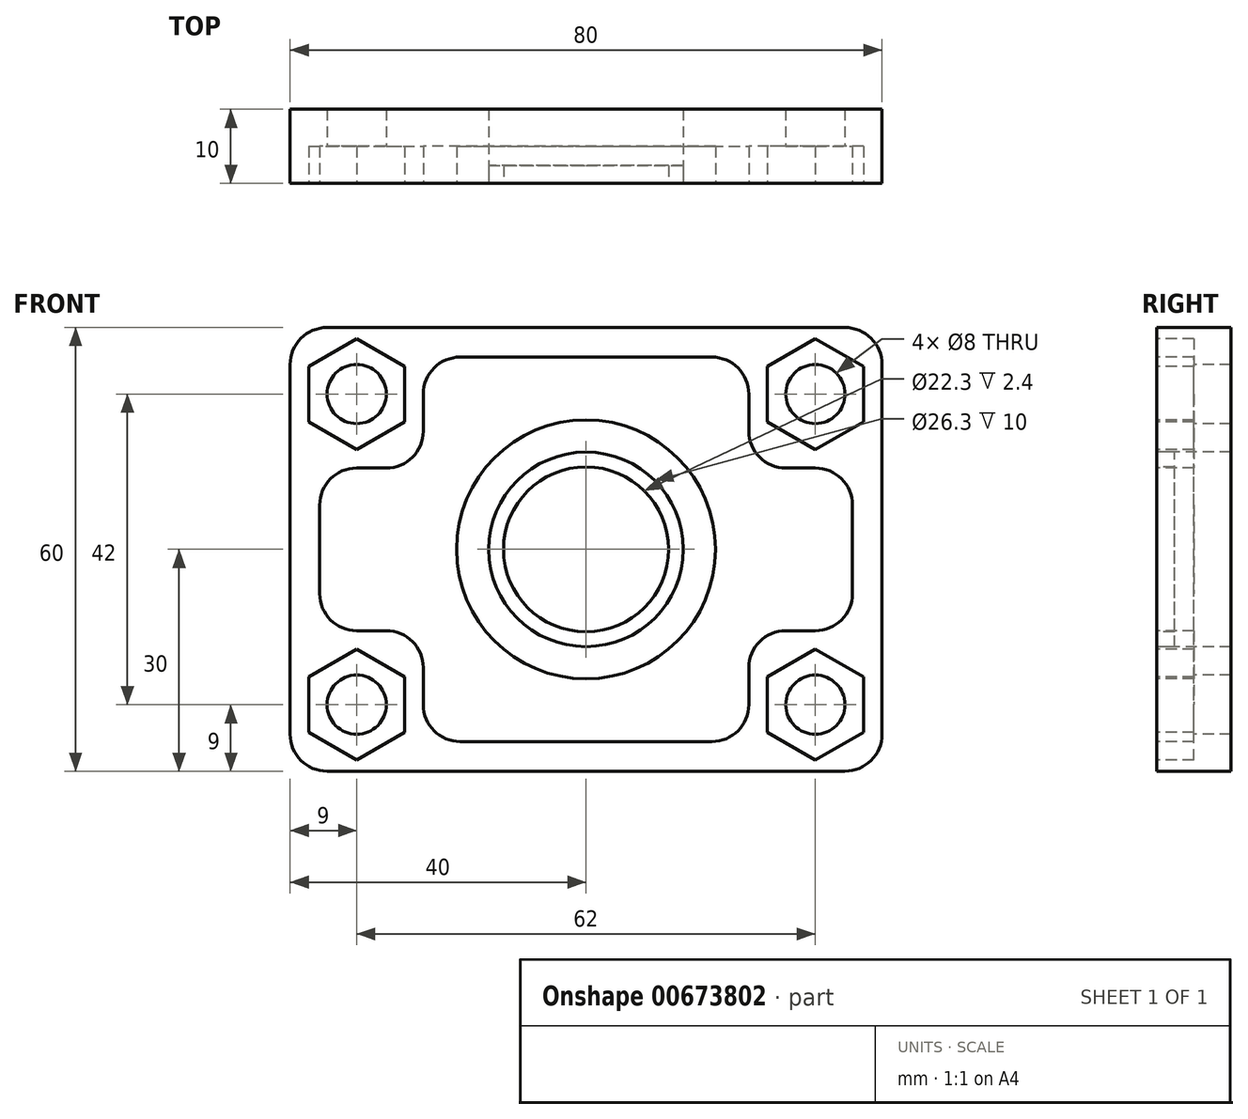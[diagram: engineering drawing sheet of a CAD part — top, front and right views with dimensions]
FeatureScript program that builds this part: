
annotation { "Feature Type Name" : "Feature", "Feature Type Description" : "" }
export const myFeature = defineFeature(function(context is Context, id is Id, definition is map)
    precondition{}
    {
        {
            var Q0;
            Q0=qCreatedBy(makeId("Front.planeOp"),FACE);
            var sketch = newSketch(context, id + "F0", { "sketchPlane" : qUnion([Q0])});
            skLineSegment(sketch, "E0.bottom", {"start": v(-40, 40) * mm, "end": v(40, 40) * mm});
            skLineSegment(sketch, "E0.top", {"start": v(-40, -20) * mm, "end": v(40, -20) * mm});
            skLineSegment(sketch, "E0.left", {"start": v(-40, 40) * mm, "end": v(-40, -20) * mm});
            skLineSegment(sketch, "E0.right", {"start": v(40, 40) * mm, "end": v(40, -20) * mm});
            skSolve(sketch);
        }
        {
            var Q0;
            Q0=qSketchRegion(id+"F0",true);
            extrude(context, id + "F1", {"entities" : qUnion([Q0]), "depth" : 10 * mm, "offsetDistance" : 25 * mm});
        }
        {
            var Q0;
            Q0=makeQuery(id+"F1.opExtrude","CAP_FACE",FACE,{"disambiguationData":[OSD([sQuery(id+"F0.wireOp",EDGE,"E0.bottom"),sQuery(id+"F0.wireOp",EDGE,"E0.top"),sQuery(id+"F0.wireOp",EDGE,"E0.left"),sQuery(id+"F0.wireOp",EDGE,"E0.right")])],"isStart":false});
            var sketch = newSketch(context, id + "F2", { "sketchPlane" : qUnion([Q0])});
            skCircle(sketch, "E1", {"center": v(0, 10) * mm, "radius": 13.15 * mm});
            skSolve(sketch);
        }
        {
            var Q0;
            Q0=qSketchRegion(id+"F2",true);
            extrude(context, id + "F3", {"entities" : qUnion([Q0]), "operationType" : NewBodyOperationType.REMOVE, "endBound" : BoundingType.THROUGH_ALL, "oppositeDirection" : true, "depth" : 25 * mm, "offsetDistance" : 25 * mm});
        }
        {
            var Q0;
            Q0=makeQuery(id+"F1.opExtrude","CAP_FACE",FACE,{"disambiguationData":[OSD([sQuery(id+"F0.wireOp",EDGE,"E0.bottom"),sQuery(id+"F0.wireOp",EDGE,"E0.top"),sQuery(id+"F0.wireOp",EDGE,"E0.left"),sQuery(id+"F0.wireOp",EDGE,"E0.right")])],"isStart":false});
            var sketch = newSketch(context, id + "F4", { "sketchPlane" : qUnion([Q0])});
            skCircle(sketch, "E2", {"center": v(-31, 31) * mm, "radius": 4 * mm});
            skCircle(sketch, "E3", {"center": v(31, 31) * mm, "radius": 4 * mm});
            skCircle(sketch, "E4", {"center": v(-31, -11) * mm, "radius": 4 * mm});
            skCircle(sketch, "E5", {"center": v(31, -11) * mm, "radius": 4 * mm});
            skSolve(sketch);
        }
        {
            var Q0;
            Q0=qSketchRegion(id+"F4",true);
            extrude(context, id + "F5", {"entities" : qUnion([Q0]), "operationType" : NewBodyOperationType.REMOVE, "endBound" : BoundingType.THROUGH_ALL, "oppositeDirection" : true, "depth" : 25 * mm, "offsetDistance" : 25 * mm});
        }
        {
            var Q0;
            Q0=makeQuery(id+"F1.opExtrude","SWEPT_EDGE",EDGE,{"disambiguationData":[OSD([sQuery(id+"F0.wireOp",EDGE,"E0.bottom"),sQuery(id+"F0.wireOp",EDGE,"E0.right")])]});
            var Q1;
            Q1=makeQuery(id+"F1.opExtrude","SWEPT_EDGE",EDGE,{"disambiguationData":[OSD([sQuery(id+"F0.wireOp",EDGE,"E0.top"),sQuery(id+"F0.wireOp",EDGE,"E0.right")])]});
            var Q2;
            Q2=makeQuery(id+"F1.opExtrude","SWEPT_EDGE",EDGE,{"disambiguationData":[OSD([sQuery(id+"F0.wireOp",EDGE,"E0.top"),sQuery(id+"F0.wireOp",EDGE,"E0.left")])]});
            var Q3;
            Q3=makeQuery(id+"F1.opExtrude","SWEPT_EDGE",EDGE,{"disambiguationData":[OSD([sQuery(id+"F0.wireOp",EDGE,"E0.bottom"),sQuery(id+"F0.wireOp",EDGE,"E0.left")])]});
            fillet(context, id + "F6", {"entities" : qUnion([Q0, Q1, Q2, Q3]), "radius" : 5 * mm, "tangentPropagation" : true, "allowEdgeOverflow" : false});
        }
        {
            var Q0;
            Q0=makeQuery(id+"F4.imprint","IMPRINT",FACE,{"disambiguationData":[TD([[makeQuery(id+"F4.imprint","IMPRINT",EDGE,{"derivedFrom":sQuery(id+"F4.wireOp",EDGE,"E2")}),-1.0]])]});
            var sketch = newSketch(context, id + "F7", { "sketchPlane" : qUnion([Q0])});
            skCircle(sketch, "E6.cCircle", {"center": v(-31, 31) * mm, "radius": 6.5 * mm, "construction": true});
            skLineSegment(sketch, "E6.0", {"start": v(-31, 38.5) * mm, "end": v(-24.5, 34.75) * mm});
            skLineSegment(sketch, "E6.1", {"start": v(-24.5, 34.75) * mm, "end": v(-24.5, 27.25) * mm});
            skLineSegment(sketch, "E6.2", {"start": v(-24.5, 27.25) * mm, "end": v(-31, 23.5) * mm});
            skLineSegment(sketch, "E6.3", {"start": v(-31, 23.5) * mm, "end": v(-37.5, 27.25) * mm});
            skLineSegment(sketch, "E6.4", {"start": v(-37.5, 27.25) * mm, "end": v(-37.5, 34.75) * mm});
            skLineSegment(sketch, "E6.5", {"start": v(-37.5, 34.75) * mm, "end": v(-31, 38.5) * mm});
            skPoint(sketch, "E6.0.midPoint", {"position": v(-27.75, 36.63) * mm});
            skCircle(sketch, "E7.cCircle", {"center": v(31, 31) * mm, "radius": 6.5 * mm, "construction": true});
            skLineSegment(sketch, "E7.0", {"start": v(24.5, 27.25) * mm, "end": v(24.5, 34.75) * mm});
            skLineSegment(sketch, "E7.1", {"start": v(24.5, 34.75) * mm, "end": v(31, 38.5) * mm});
            skLineSegment(sketch, "E7.2", {"start": v(31, 38.5) * mm, "end": v(37.5, 34.75) * mm});
            skLineSegment(sketch, "E7.3", {"start": v(37.5, 34.75) * mm, "end": v(37.5, 27.25) * mm});
            skLineSegment(sketch, "E7.4", {"start": v(37.5, 27.25) * mm, "end": v(31, 23.5) * mm});
            skLineSegment(sketch, "E7.5", {"start": v(31, 23.5) * mm, "end": v(24.5, 27.25) * mm});
            skPoint(sketch, "E7.0.midPoint", {"position": v(24.5, 31) * mm});
            skCircle(sketch, "E8.cCircle", {"center": v(31, -11) * mm, "radius": 6.5 * mm, "construction": true});
            skLineSegment(sketch, "E8.0", {"start": v(24.5, -14.75) * mm, "end": v(24.5, -7.25) * mm});
            skLineSegment(sketch, "E8.1", {"start": v(24.5, -7.25) * mm, "end": v(31, -3.5) * mm});
            skLineSegment(sketch, "E8.2", {"start": v(31, -3.5) * mm, "end": v(37.5, -7.25) * mm});
            skLineSegment(sketch, "E8.3", {"start": v(37.5, -7.25) * mm, "end": v(37.5, -14.75) * mm});
            skLineSegment(sketch, "E8.4", {"start": v(37.5, -14.75) * mm, "end": v(31, -18.5) * mm});
            skLineSegment(sketch, "E8.5", {"start": v(31, -18.5) * mm, "end": v(24.5, -14.75) * mm});
            skPoint(sketch, "E8.0.midPoint", {"position": v(24.5, -11) * mm});
            skCircle(sketch, "E9.cCircle", {"center": v(-31, -11) * mm, "radius": 6.5 * mm, "construction": true});
            skLineSegment(sketch, "E9.0", {"start": v(-31, -3.5) * mm, "end": v(-24.5, -7.25) * mm});
            skLineSegment(sketch, "E9.1", {"start": v(-24.5, -7.25) * mm, "end": v(-24.5, -14.75) * mm});
            skLineSegment(sketch, "E9.2", {"start": v(-24.5, -14.75) * mm, "end": v(-31, -18.5) * mm});
            skLineSegment(sketch, "E9.3", {"start": v(-31, -18.5) * mm, "end": v(-37.5, -14.75) * mm});
            skLineSegment(sketch, "E9.4", {"start": v(-37.5, -14.75) * mm, "end": v(-37.5, -7.25) * mm});
            skLineSegment(sketch, "E9.5", {"start": v(-37.5, -7.25) * mm, "end": v(-31, -3.5) * mm});
            skPoint(sketch, "E9.0.midPoint", {"position": v(-27.75, -5.37) * mm});
            skCircle(sketch, "E10", {"center": v(0, 10) * mm, "radius": 17.5 * mm});
            skLineSegment(sketch, "E11.bottom", {"start": v(-22, 36) * mm, "end": v(22, 36) * mm});
            skLineSegment(sketch, "E11.top", {"start": v(-22, -16) * mm, "end": v(22, -16) * mm});
            skLineSegment(sketch, "E11.left", {"start": v(-22, 36) * mm, "end": v(-22, -16) * mm});
            skLineSegment(sketch, "E11.right", {"start": v(22, 36) * mm, "end": v(22, -16) * mm});
            skLineSegment(sketch, "E12.bottom", {"start": v(36, 21) * mm, "end": v(-36, 21) * mm});
            skLineSegment(sketch, "E12.top", {"start": v(36, -1) * mm, "end": v(-36, -1) * mm});
            skLineSegment(sketch, "E12.left", {"start": v(36, 21) * mm, "end": v(36, -1) * mm});
            skLineSegment(sketch, "E12.right", {"start": v(-36, 21) * mm, "end": v(-36, -1) * mm});
            skSolve(sketch);
        }
        {
            var Q0;
            Q0=qSketchRegion(id+"F7",true);
            extrude(context, id + "F8", {"entities" : qUnion([Q0]), "operationType" : NewBodyOperationType.REMOVE, "oppositeDirection" : true, "depth" : 5 * mm, "offsetDistance" : 25 * mm});
        }
        {
            var Q0;
            Q0=makeQuery(id+"F8.boolean.opBoolean","COPY",EDGE,{"derivedFrom":makeQuery(id+"F8.opExtrude","SWEPT_EDGE",EDGE,{"disambiguationData":[OSD([sQuery(id+"F7.wireOp",EDGE,"E11.left"),sQuery(id+"F7.wireOp",EDGE,"E12.bottom")])]})});
            var Q1;
            Q1=makeQuery(id+"F8.boolean.opBoolean","COPY",EDGE,{"derivedFrom":makeQuery(id+"F8.opExtrude","SWEPT_EDGE",EDGE,{"disambiguationData":[OSD([sQuery(id+"F7.wireOp",EDGE,"E12.bottom"),sQuery(id+"F7.wireOp",EDGE,"E12.right")])]})});
            var Q2;
            Q2=makeQuery(id+"F8.boolean.opBoolean","COPY",EDGE,{"derivedFrom":makeQuery(id+"F8.opExtrude","SWEPT_EDGE",EDGE,{"disambiguationData":[OSD([sQuery(id+"F7.wireOp",EDGE,"E11.bottom"),sQuery(id+"F7.wireOp",EDGE,"E11.left")])]})});
            var Q3;
            Q3=makeQuery(id+"F8.boolean.opBoolean","COPY",EDGE,{"derivedFrom":makeQuery(id+"F8.opExtrude","SWEPT_EDGE",EDGE,{"disambiguationData":[OSD([sQuery(id+"F7.wireOp",EDGE,"E11.bottom"),sQuery(id+"F7.wireOp",EDGE,"E11.right")])]})});
            var Q4;
            Q4=makeQuery(id+"F8.boolean.opBoolean","COPY",EDGE,{"derivedFrom":makeQuery(id+"F8.opExtrude","SWEPT_EDGE",EDGE,{"disambiguationData":[OSD([sQuery(id+"F7.wireOp",EDGE,"E11.right"),sQuery(id+"F7.wireOp",EDGE,"E12.bottom")])]})});
            var Q5;
            Q5=makeQuery(id+"F8.boolean.opBoolean","COPY",EDGE,{"derivedFrom":makeQuery(id+"F8.opExtrude","SWEPT_EDGE",EDGE,{"disambiguationData":[OSD([sQuery(id+"F7.wireOp",EDGE,"E12.bottom"),sQuery(id+"F7.wireOp",EDGE,"E12.left")])]})});
            var Q6;
            Q6=makeQuery(id+"F8.boolean.opBoolean","COPY",EDGE,{"derivedFrom":makeQuery(id+"F8.opExtrude","SWEPT_EDGE",EDGE,{"disambiguationData":[OSD([sQuery(id+"F7.wireOp",EDGE,"E12.top"),sQuery(id+"F7.wireOp",EDGE,"E12.right")])]})});
            var Q7;
            Q7=makeQuery(id+"F8.boolean.opBoolean","COPY",EDGE,{"derivedFrom":makeQuery(id+"F8.opExtrude","SWEPT_EDGE",EDGE,{"disambiguationData":[OSD([sQuery(id+"F7.wireOp",EDGE,"E11.left"),sQuery(id+"F7.wireOp",EDGE,"E12.top")])]})});
            var Q8;
            Q8=makeQuery(id+"F8.boolean.opBoolean","COPY",EDGE,{"derivedFrom":makeQuery(id+"F8.opExtrude","SWEPT_EDGE",EDGE,{"disambiguationData":[OSD([sQuery(id+"F7.wireOp",EDGE,"E11.top"),sQuery(id+"F7.wireOp",EDGE,"E11.left")])]})});
            var Q9;
            Q9=makeQuery(id+"F8.boolean.opBoolean","COPY",EDGE,{"derivedFrom":makeQuery(id+"F8.opExtrude","SWEPT_EDGE",EDGE,{"disambiguationData":[OSD([sQuery(id+"F7.wireOp",EDGE,"E12.top"),sQuery(id+"F7.wireOp",EDGE,"E12.left")])]})});
            var Q10;
            Q10=makeQuery(id+"F8.boolean.opBoolean","COPY",EDGE,{"derivedFrom":makeQuery(id+"F8.opExtrude","SWEPT_EDGE",EDGE,{"disambiguationData":[OSD([sQuery(id+"F7.wireOp",EDGE,"E11.right"),sQuery(id+"F7.wireOp",EDGE,"E12.top")])]})});
            var Q11;
            Q11=makeQuery(id+"F8.boolean.opBoolean","COPY",EDGE,{"derivedFrom":makeQuery(id+"F8.opExtrude","SWEPT_EDGE",EDGE,{"disambiguationData":[OSD([sQuery(id+"F7.wireOp",EDGE,"E11.top"),sQuery(id+"F7.wireOp",EDGE,"E11.right")])]})});
            fillet(context, id + "F9", {"entities" : qUnion([Q0, Q1, Q2, Q3, Q4, Q5, Q6, Q7, Q8, Q9, Q10, Q11]), "radius" : 5 * mm, "tangentPropagation" : true, "allowEdgeOverflow" : false});
        }
        {
            var Q0;
            Q0=makeQuery(id+"F8.boolean.opBoolean","SPLIT",FACE,{"disambiguationData":[TD([makeQuery(id+"F3.boolean.opBoolean","COPY",FACE,{"derivedFrom":makeQuery(id+"F3.opExtrude","SWEPT_FACE",FACE,{"disambiguationData":[OSD([sQuery(id+"F2.wireOp",EDGE,"E1")])]})})])],"derivedFrom":makeQuery(id+"F1.opExtrude","CAP_FACE",FACE,{"disambiguationData":[OSD([sQuery(id+"F0.wireOp",EDGE,"E0.bottom"),sQuery(id+"F0.wireOp",EDGE,"E0.top"),sQuery(id+"F0.wireOp",EDGE,"E0.left"),sQuery(id+"F0.wireOp",EDGE,"E0.right")])],"isStart":false})});
            var sketch = newSketch(context, id + "F10", { "sketchPlane" : qUnion([Q0])});
            skCircle(sketch, "E13", {"center": v(0, 10) * mm, "radius": 11.15 * mm});
            skSolve(sketch);
        }
        {
            var Q0;
            Q0=makeQuery(id+"F10.imprint","IMPRINT",FACE,{"disambiguationData":[TD([[makeQuery(id+"F10.imprint","IMPRINT",EDGE,{"derivedFrom":sQuery(id+"F10.wireOp",EDGE,"E13")}),-1.0]])]});
            extrude(context, id + "F11", {"entities" : qUnion([Q0]), "oppositeDirection" : true, "depth" : 2.4 * mm, "offsetDistance" : 25 * mm});
        }
    });
